# Revit family: Faucet-Wall_Mount-Lavatory-KOHLER-Purist-K-14415IN+1
name_source: partatom
category: Plumbing Fixtures
revit_build: Autodesk Revit 2017 (Build: 20160225_1515(x64)
units: mm (PartAtom-declared; Revit-internal decimal feet)

## family parameters
Cut with Voids When Loaded = No
Host = Face
OmniClass Number = 23.31.11.00
OmniClass Title = Faucets
Part Type = Normal
Room Calculation Point = No
Round Connector Dimension = Use Diameter
Shared = No

## types (2) — shared parameters
ADA Compliant = No
Assembly Code = D2010
CW Connection = Yes
Cold Water Inlet = Cold Water Inlet
Date Modified = 08/21/2020
Default Elevation = 36"
Description = Wall-mount lavatory faucet (Valve is included)
Drain Included = Yes
Faucet Hole Spacing = 7 7/8"
Finish = Kohler-Metal-CP-Polished_Chrome
Flow Rate = 0 GPM
HW Connection = Yes
Height = 2"
Hot Water Inlet = Hot Water Inlet
Length = 8 1/4"
Manufacturer = KOHLER Co.
Master Format 2014 = 22 41 39
Master Format 2014 Name = Residential Faucets, Supplies, and Trim
Material = Premium Metal Construction
Pressure = 0.00 psi
Product Name = Purist
Spout Reach = 8 1/4"
URL = https://www.kohler.co.in
Vent Connection = No
Waste Connection = No
Waste Water Outlet = Waste Water Outlet
WaterSense Certified = No
Width = 7 7/8"

## per-type parameters (varying)
| type | Cross Handle | Handle Clearance | Handle Height | Lever Handle | Model | Product Documentation Link | Product Page URL | Type |
| Cross Handle, CP-Polished Chrome | Yes | 1 1/2" | 3 7/16" | No | K-14415IN-3ND-CP |  |  | 1 |
| Lever Handle, CP-Polished Chrome | No | 2 3/16" | 3 1/2" | Yes | K-14415IN-4ND-CP | http://resources.kohler.com | https://www.kohler.co.in | 2 |

## geometry (parser evidence)
native form markers: Sweep x6
no freeform markers — native parametric forms only
